# Revit family: 6542 A-Chair Metal Base
name_source: partatom
category: Furniture
revit_build: Autodesk Revit 2017 (Build: 20171027_0315(x64)
units: mm (PartAtom-declared; Revit-internal decimal feet)

## family parameters
Always vertical = Yes
Cut with Voids When Loaded = No
OmniClass Number = 23.40.20.00
OmniClass Title = General Furniture and Specialties
Room Calculation Point = No
Shared = No
Work Plane-Based = No

## types (1)
- 6542 A-Chair Metal Base
    Depth = 87 cm
    Description = Originally designed by Jens Risom in 1961 the A-Chair is a graceful expression of an elegant, upholstered chair in a timeless design, boasting an A-frame in the back for added support and as signature detail. The curved lines of the two-piece back and loose seat cushion accentuate the comfort and softness of this foam-filled chair with a base available in solid oak, walnut, black lacquered steel or matt chrome.
    Design year = 1961
    Designer = Jens Risom
    Height = 87 cm
    Item No. = 6540
    Legs = FF Steel Black
    Manufacturer = Fredericia Furniture
    Model = A-Chair Wood Base
    Seat = FF Sunniva 717
    Seat Height = 42 cm
    Shell = FF Sunniva 717
    URL = https://www.fredericia.com
    Variation Legs = Available in other kind of wood
    Variations Upholster = Available in fabric and leather
    Weight = 23kg
    Width = 78 cm

## geometry (parser evidence)
native form markers: Sweep x2
no freeform markers — native parametric forms only
